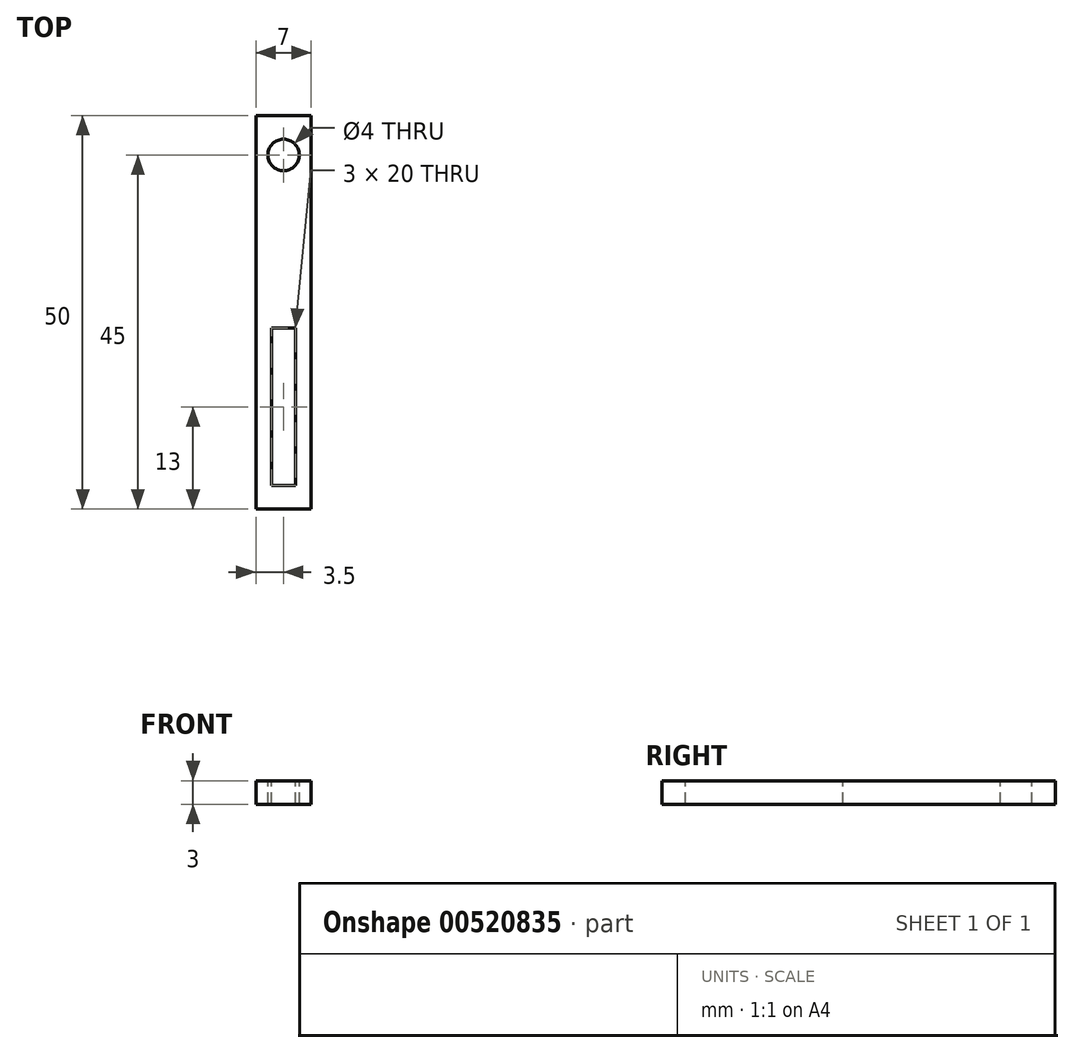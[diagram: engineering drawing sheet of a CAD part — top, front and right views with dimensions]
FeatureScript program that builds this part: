
annotation { "Feature Type Name" : "Feature", "Feature Type Description" : "" }
export const myFeature = defineFeature(function(context is Context, id is Id, definition is map)
    precondition{}
    {
        {
            var Q0;
            Q0=qCreatedBy(makeId("Top.planeOp"),FACE);
            var sketch = newSketch(context, id + "F0", { "sketchPlane" : qUnion([Q0])});
            skLineSegment(sketch, "E0.bottom", {"start": v(0, 0) * mm, "end": v(7, 0) * mm});
            skLineSegment(sketch, "E0.top", {"start": v(0, 50) * mm, "end": v(7, 50) * mm});
            skLineSegment(sketch, "E0.left", {"start": v(0, 0) * mm, "end": v(0, 50) * mm});
            skLineSegment(sketch, "E0.right", {"start": v(7, 0) * mm, "end": v(7, 50) * mm});
            skSolve(sketch);
        }
        {
            var Q0;
            Q0 = qSketchRegion(id + "F0", true);
            extrude(context, id + "F1", {"entities" : qUnion([Q0]), "depth" : 3 * mm, "offsetDistance" : 25 * mm});
        }
        {
            var Q0;
            Q0=makeQuery(id+"F1.opExtrude","CAP_FACE",FACE,{"disambiguationData":[OSD([sQuery(id+"F0.wireOp",EDGE,"E0.bottom"),sQuery(id+"F0.wireOp",EDGE,"E0.top"),sQuery(id+"F0.wireOp",EDGE,"E0.left"),sQuery(id+"F0.wireOp",EDGE,"E0.right")])],"isStart":false});
            var sketch = newSketch(context, id + "F2", { "sketchPlane" : qUnion([Q0])});
            skLineSegment(sketch, "E1.bottom", {"start": v(2, 23) * mm, "end": v(5, 23) * mm});
            skLineSegment(sketch, "E1.top", {"start": v(2, 3) * mm, "end": v(5, 3) * mm});
            skLineSegment(sketch, "E1.left", {"start": v(2, 23) * mm, "end": v(2, 3) * mm});
            skLineSegment(sketch, "E1.right", {"start": v(5, 23) * mm, "end": v(5, 3) * mm});
            skCircle(sketch, "E2", {"center": v(3.5, 45) * mm, "radius": 2 * mm});
            skPoint(sketch, "E2.centerSnap0", {"position": v(3.5, 50) * mm});
            skSolve(sketch);
        }
        {
            var Q0;
            Q0 = qSketchRegion(id + "F2", true);
            extrude(context, id + "F3", {"entities" : qUnion([Q0]), "operationType" : NewBodyOperationType.REMOVE, "endBound" : BoundingType.THROUGH_ALL, "oppositeDirection" : true, "depth" : 25 * mm, "offsetDistance" : 25 * mm});
        }
    });
